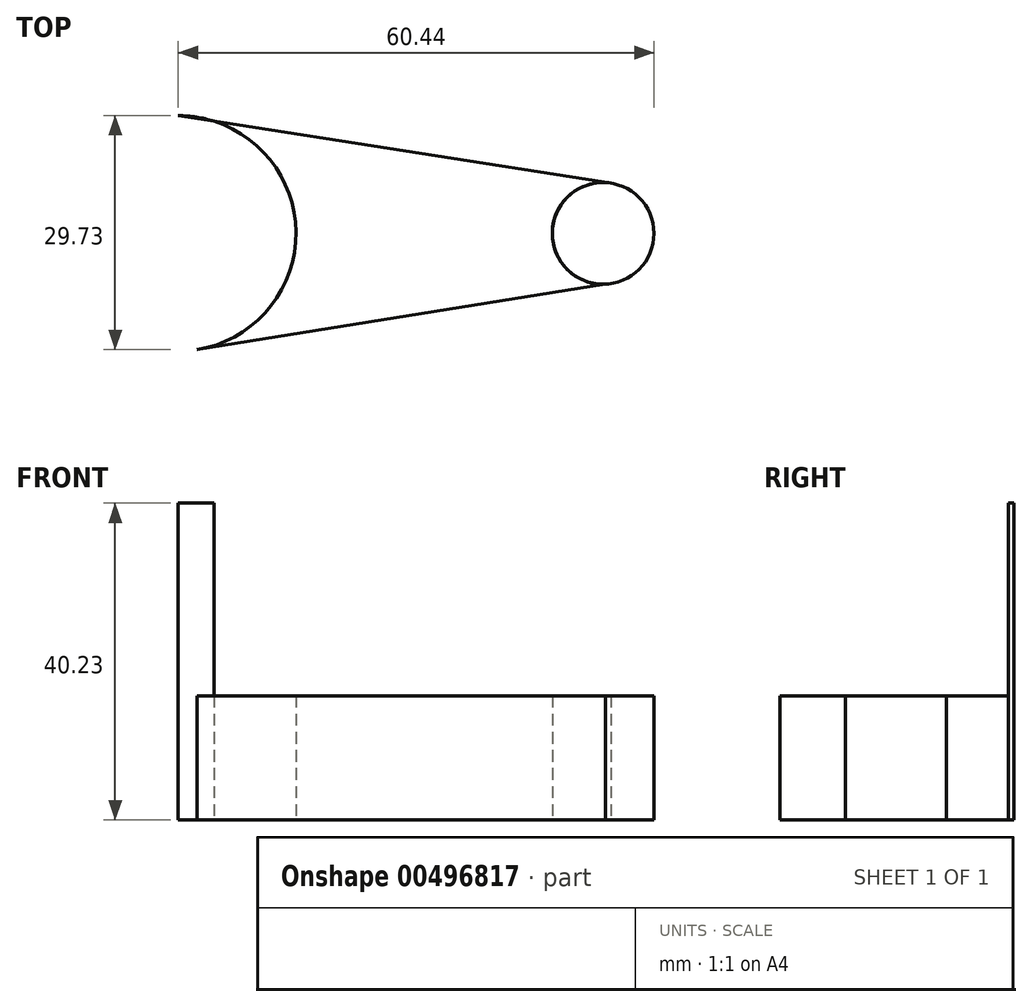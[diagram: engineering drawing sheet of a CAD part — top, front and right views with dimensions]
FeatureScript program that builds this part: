
annotation { "Feature Type Name" : "Feature", "Feature Type Description" : "" }
export const myFeature = defineFeature(function(context is Context, id is Id, definition is map)
    precondition{}
    {
        {
            var Q0;
            Q0=qCreatedBy(makeId("Top.planeOp"),FACE);
            var sketch = newSketch(context, id + "F0", { "sketchPlane" : qUnion([Q0])});
            skCircle(sketch, "E0", {"center": v(53.98, 0) * mm, "radius": 6.46 * mm});
            skCircle(sketch, "E1", {"center": v(0, 0) * mm, "radius": 14.96 * mm});
            skLineSegment(sketch, "E2", {"start": v(54.24, -6.46) * mm, "end": v(0, -15.15) * mm});
            skLineSegment(sketch, "E3", {"start": v(0, 14.96) * mm, "end": v(54.97, 6.38) * mm});
            skSolve(sketch);
        }
        {
            var Q0;
            {var subQ0=sQuery(id+"F0.wireOp",EDGE,"E2");var subQ1=sQuery(id+"F0.wireOp",EDGE,"E0");var subQ2=makeQuery(id+"F0.imprint","INTERSECT",VERTEX,{"derivedFrom":[subQ1,subQ0]});Q0=makeQuery(id+"F0.imprint","IMPRINT",FACE,{"disambiguationData":[TD([[makeQuery(id+"F0.imprint","IMPRINT",EDGE,{"disambiguationData":[TD([[subQ2,1.0]])],"derivedFrom":subQ1}),-1.0]])]});}
            var sketch = newSketch(context, id + "F1", { "sketchPlane" : qUnion([Q0])});
            skSolve(sketch);
        }
        {
            var Q0;
            {var subQ0=sQuery(id+"F0.wireOp",EDGE,"E0");var subQ1=makeQuery(id+"F0.imprint","INTERSECT",VERTEX,{"derivedFrom":[subQ0,sQuery(id+"F0.wireOp",EDGE,"E2")]});Q0=makeQuery(id+"F0.imprint","IMPRINT",FACE,{"disambiguationData":[TD([[makeQuery(id+"F0.imprint","IMPRINT",EDGE,{"disambiguationData":[TD([[subQ1,1.0]])],"derivedFrom":subQ0}),1.0]])]});}
            var sketch = newSketch(context, id + "F2", { "sketchPlane" : qUnion([Q0])});
            skSolve(sketch);
        }
        {
            var Q0;
            {var subQ0=sQuery(id+"F0.wireOp",EDGE,"E2");var subQ1=sQuery(id+"F0.wireOp",EDGE,"E0");var subQ2=makeQuery(id+"F0.imprint","INTERSECT",VERTEX,{"derivedFrom":[subQ1,subQ0]});Q0=makeQuery(id+"F1.imprint","IMPRINT",FACE,{"disambiguationData":[TD([[makeQuery(id+"F1.imprint","IMPRINT",EDGE,{"derivedFrom":makeQuery(id+"F0.imprint","IMPRINT",EDGE,{"disambiguationData":[TD([[subQ2,1.0]])],"derivedFrom":subQ1})}),-1.0]])]});}
            var Q1;
            {var subQ0=sQuery(id+"F0.wireOp",EDGE,"E0");var subQ1=makeQuery(id+"F0.imprint","INTERSECT",VERTEX,{"derivedFrom":[subQ0,sQuery(id+"F0.wireOp",EDGE,"E2")]});Q1=makeQuery(id+"F2.imprint","IMPRINT",FACE,{"disambiguationData":[TD([[makeQuery(id+"F2.imprint","IMPRINT",EDGE,{"derivedFrom":makeQuery(id+"F0.imprint","IMPRINT",EDGE,{"disambiguationData":[TD([[subQ1,1.0]])],"derivedFrom":subQ0})}),1.0]])]});}
            extrude(context, id + "F3", {"entities" : qUnion([Q0, Q1]), "depth" : 15.77 * mm});
        }
        {
            var Q0;
            {var subQ0=sQuery(id+"F0.wireOp",EDGE,"E3");var subQ1=sQuery(id+"F0.wireOp",EDGE,"E1");var subQ2=makeQuery(id+"F0.imprint","INTERSECT",VERTEX,{"disambiguationData":[OD(0.0)],"derivedFrom":[subQ1,subQ0]});Q0=makeQuery(id+"F0.imprint","IMPRINT",FACE,{"disambiguationData":[TD([[makeQuery(id+"F0.imprint","IMPRINT",EDGE,{"disambiguationData":[TD([[subQ2,-1.0]])],"derivedFrom":subQ1}),1.0]])]});}
            extrude(context, id + "F4", {"entities" : qUnion([Q0]), "operationType" : NewBodyOperationType.ADD, "depth" : 40.23 * mm});
        }
    });
